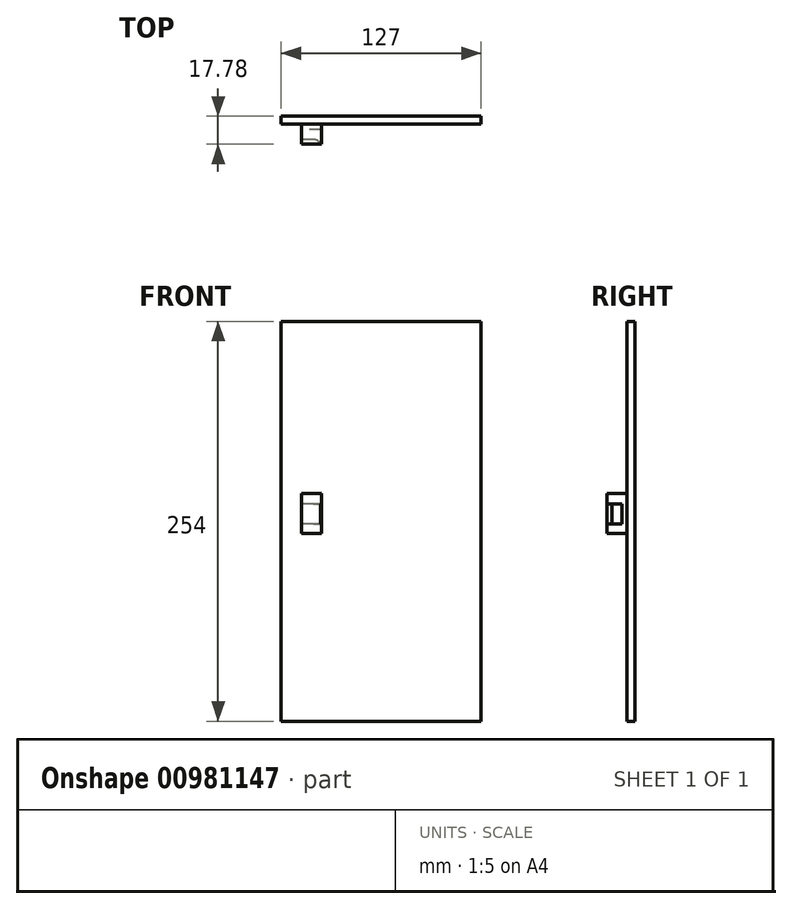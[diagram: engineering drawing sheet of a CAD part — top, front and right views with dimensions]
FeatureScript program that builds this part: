
annotation { "Feature Type Name" : "Feature", "Feature Type Description" : "" }
export const myFeature = defineFeature(function(context is Context, id is Id, definition is map)
    precondition{}
    {
        {
            var Q0;
            Q0=qCreatedBy(makeId("Front.planeOp"),FACE);
            var sketch = newSketch(context, id + "F0", { "sketchPlane" : qUnion([Q0])});
            skLineSegment(sketch, "E0.bottom", {"start": v(63.5, -132.02) * mm, "end": v(-63.5, -132.02) * mm});
            skLineSegment(sketch, "E0.top", {"start": v(63.5, 121.98) * mm, "end": v(-63.5, 121.98) * mm});
            skLineSegment(sketch, "E0.left", {"start": v(63.5, -132.02) * mm, "end": v(63.5, 121.98) * mm});
            skLineSegment(sketch, "E0.right", {"start": v(-63.5, -132.02) * mm, "end": v(-63.5, 121.98) * mm});
            skPoint(sketch, "E0.middle", {"position": v(0, -5.02) * mm});
            skSolve(sketch);
        }
        {
            var Q0;
            Q0=makeQuery(id+"F0.imprint","IMPRINT",FACE,{"disambiguationData":[TD([[makeQuery(id+"F0.imprint","IMPRINT",EDGE,{"derivedFrom":sQuery(id+"F0.wireOp",EDGE,"E0.bottom")}),-1.0]])]});
            extrude(context, id + "F1", {"entities" : qUnion([Q0]), "endBound" : BoundingType.SYMMETRIC, "depth" : 5.08 * mm, "offsetDistance" : 25.4 * mm});
        }
        {
            var Q0;
            Q0=makeQuery(id+"F1.opExtrude","CAP_FACE",FACE,{"disambiguationData":[OSD([sQuery(id+"F0.wireOp",EDGE,"E0.bottom"),sQuery(id+"F0.wireOp",EDGE,"E0.top"),sQuery(id+"F0.wireOp",EDGE,"E0.left"),sQuery(id+"F0.wireOp",EDGE,"E0.right")])],"isStart":false});
            var sketch = newSketch(context, id + "F2", { "sketchPlane" : qUnion([Q0])});
            skLineSegment(sketch, "E1.bottom", {"start": v(-50.67, 12.7) * mm, "end": v(-37.97, 12.7) * mm});
            skLineSegment(sketch, "E1.top", {"start": v(-50.67, -12.7) * mm, "end": v(-37.97, -12.7) * mm});
            skLineSegment(sketch, "E1.left", {"start": v(-50.67, 12.7) * mm, "end": v(-50.67, -12.7) * mm});
            skLineSegment(sketch, "E1.right", {"start": v(-37.97, 12.7) * mm, "end": v(-37.97, -12.7) * mm});
            skSolve(sketch);
        }
        {
            var Q0;
            Q0 = qSketchRegion(id + "F2", true);
            extrude(context, id + "F3", {"entities" : qUnion([Q0]), "operationType" : NewBodyOperationType.ADD, "depth" : 12.7 * mm, "offsetDistance" : 25.4 * mm});
        }
        {
            var Q0;
            Q0=makeQuery(id+"F3.opExtrude","SWEPT_FACE",FACE,{"disambiguationData":[OSD([sQuery(id+"F2.wireOp",EDGE,"E1.left")])]});
            var sketch = newSketch(context, id + "F4", { "sketchPlane" : qUnion([Q0])});
            skLineSegment(sketch, "E2.bottom", {"start": v(5.77, 5.92) * mm, "end": v(12.12, 5.92) * mm});
            skLineSegment(sketch, "E2.top", {"start": v(5.77, -6.78) * mm, "end": v(12.12, -6.78) * mm});
            skLineSegment(sketch, "E2.left", {"start": v(5.77, 5.92) * mm, "end": v(5.77, -6.78) * mm});
            skLineSegment(sketch, "E2.right", {"start": v(12.12, 5.92) * mm, "end": v(12.12, -6.78) * mm});
            skSolve(sketch);
        }
        {
            var Q0;
            Q0 = qSketchRegion(id + "F4", true);
            extrude(context, id + "F5", {"entities" : qUnion([Q0]), "operationType" : NewBodyOperationType.REMOVE, "oppositeDirection" : true, "depth" : 25.4 * mm, "offsetDistance" : 25.4 * mm});
        }
        {
            var Q0;
            Q0=makeQuery(id+"F5.boolean.opBoolean","COPY",EDGE,{"derivedFrom":makeQuery(id+"F5.opExtrude","CAP_EDGE",EDGE,{"disambiguationData":[OSD([sQuery(id+"F4.wireOp",EDGE,"E2.right")])],"isStart":true})});
            var Q1;
            Q1=makeQuery(id+"F5.boolean.opBoolean","INTERSECT",EDGE,{"derivedFrom":[makeQuery(id+"F3.opExtrude","SWEPT_FACE",FACE,{"disambiguationData":[OSD([sQuery(id+"F2.wireOp",EDGE,"E1.right")])]}),makeQuery(id+"F5.opExtrude","SWEPT_FACE",FACE,{"disambiguationData":[OSD([sQuery(id+"F4.wireOp",EDGE,"E2.right")])]})]});
            fillet(context, id + "F6", {"entities" : qUnion([Q0, Q1]), "radius" : 5.08 * mm, "tangentPropagation" : true, "allowEdgeOverflow" : false});
        }
    });
